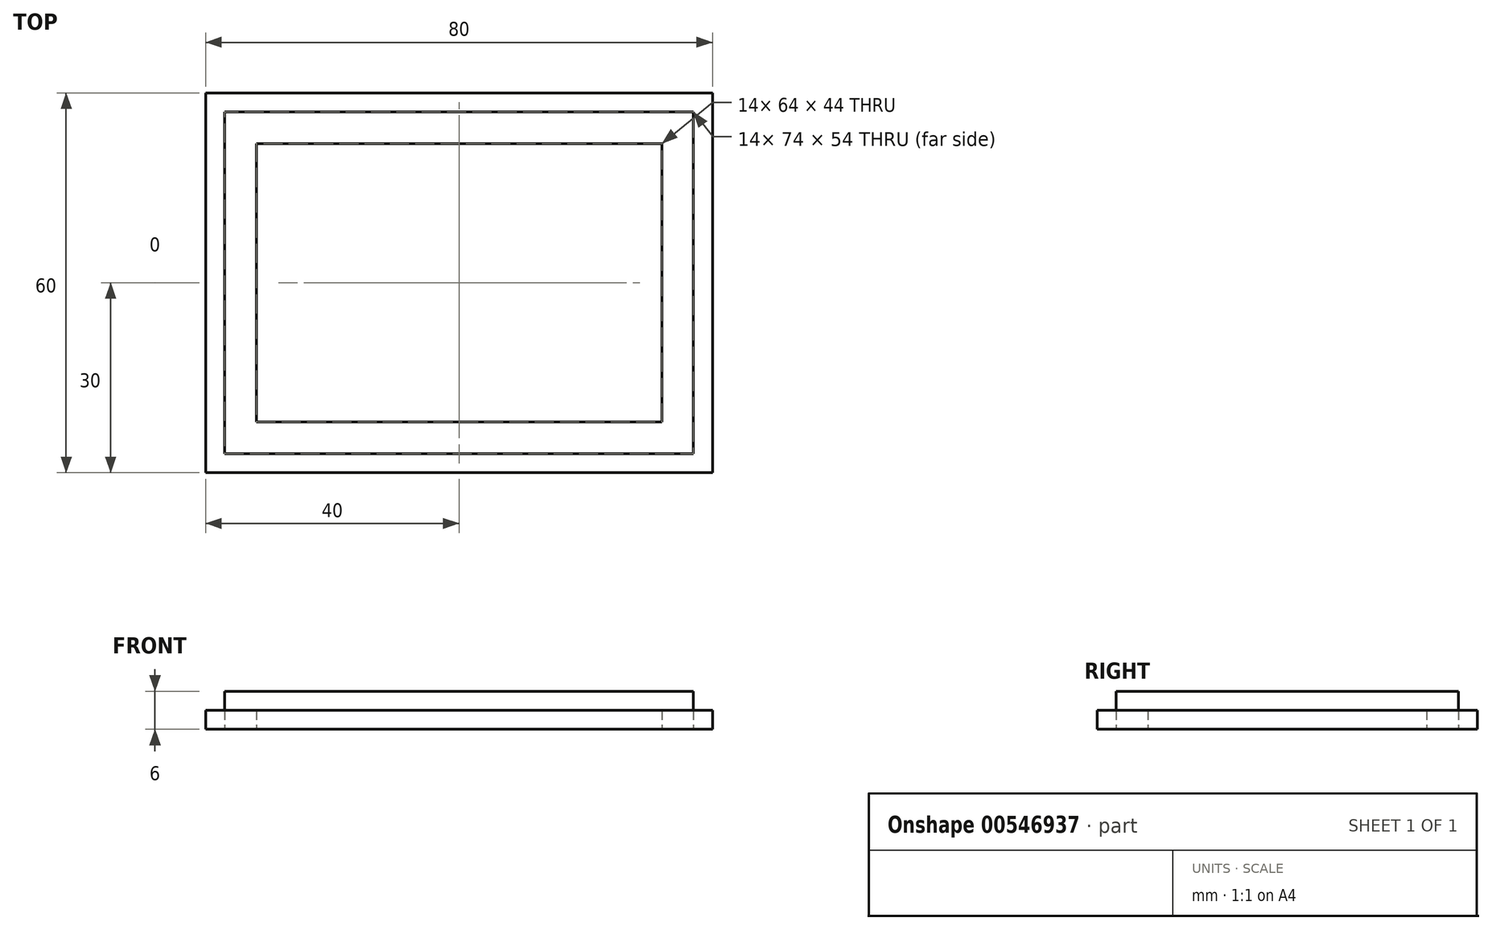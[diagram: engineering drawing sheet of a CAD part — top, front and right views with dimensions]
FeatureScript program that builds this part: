
annotation { "Feature Type Name" : "Feature", "Feature Type Description" : "" }
export const myFeature = defineFeature(function(context is Context, id is Id, definition is map)
    precondition{}
    {
        {
            var Q0;
            Q0=qCreatedBy(makeId("Top.planeOp"),FACE);
            var sketch = newSketch(context, id + "F0", { "sketchPlane" : qUnion([Q0])});
            skLineSegment(sketch, "E0.bottom", {"start": v(0, 0) * mm, "end": v(80, 0) * mm});
            skLineSegment(sketch, "E0.top", {"start": v(0, 60) * mm, "end": v(80, 60) * mm});
            skLineSegment(sketch, "E0.left", {"start": v(0, 0) * mm, "end": v(0, 60) * mm});
            skLineSegment(sketch, "E0.right", {"start": v(80, 0) * mm, "end": v(80, 60) * mm});
            skLineSegment(sketch, "E1", {"start": v(0, 0) * mm, "end": v(0, 3) * mm, "construction": true});
            skLineSegment(sketch, "E2", {"start": v(0, 3) * mm, "end": v(3, 3) * mm, "construction": true});
            skLineSegment(sketch, "E3", {"start": v(3, 3) * mm, "end": v(3, 8) * mm, "construction": true});
            skLineSegment(sketch, "E4", {"start": v(3, 8) * mm, "end": v(8, 8) * mm, "construction": true});
            skLineSegment(sketch, "E5.bottom", {"start": v(3, 3) * mm, "end": v(77, 3) * mm});
            skLineSegment(sketch, "E5.top", {"start": v(3, 57) * mm, "end": v(77, 57) * mm});
            skLineSegment(sketch, "E5.left", {"start": v(3, 3) * mm, "end": v(3, 57) * mm});
            skLineSegment(sketch, "E5.right", {"start": v(77, 3) * mm, "end": v(77, 57) * mm});
            skLineSegment(sketch, "E6.bottom", {"start": v(8, 8) * mm, "end": v(72, 8) * mm});
            skLineSegment(sketch, "E6.top", {"start": v(8, 52) * mm, "end": v(72, 52) * mm});
            skLineSegment(sketch, "E6.left", {"start": v(8, 8) * mm, "end": v(8, 52) * mm});
            skLineSegment(sketch, "E6.right", {"start": v(72, 8) * mm, "end": v(72, 52) * mm});
            skSolve(sketch);
        }
        {
            var Q0;
            Q0=makeQuery(id+"F0.imprint","IMPRINT",FACE,{"disambiguationData":[TD([[makeQuery(id+"F0.imprint","IMPRINT",EDGE,{"derivedFrom":sQuery(id+"F0.wireOp",EDGE,"E6.bottom")}),1.0]])]});
            var Q1;
            Q1=makeQuery(id+"F0.imprint","IMPRINT",FACE,{"disambiguationData":[TD([[makeQuery(id+"F0.imprint","IMPRINT",EDGE,{"derivedFrom":sQuery(id+"F0.wireOp",EDGE,"E0.bottom")}),1.0]])]});
            extrude(context, id + "F1", {"entities" : qUnion([Q0, Q1]), "depth" : 3 * mm, "offsetDistance" : 25 * mm});
        }
        {
            var Q0;
            Q0=makeQuery(id+"F0.imprint","IMPRINT",FACE,{"disambiguationData":[TD([[makeQuery(id+"F0.imprint","IMPRINT",EDGE,{"derivedFrom":sQuery(id+"F0.wireOp",EDGE,"E5.bottom")}),1.0]])]});
            extrude(context, id + "F2", {"entities" : qUnion([Q0]), "depth" : 6 * mm, "offsetDistance" : 25 * mm});
        }
    });
